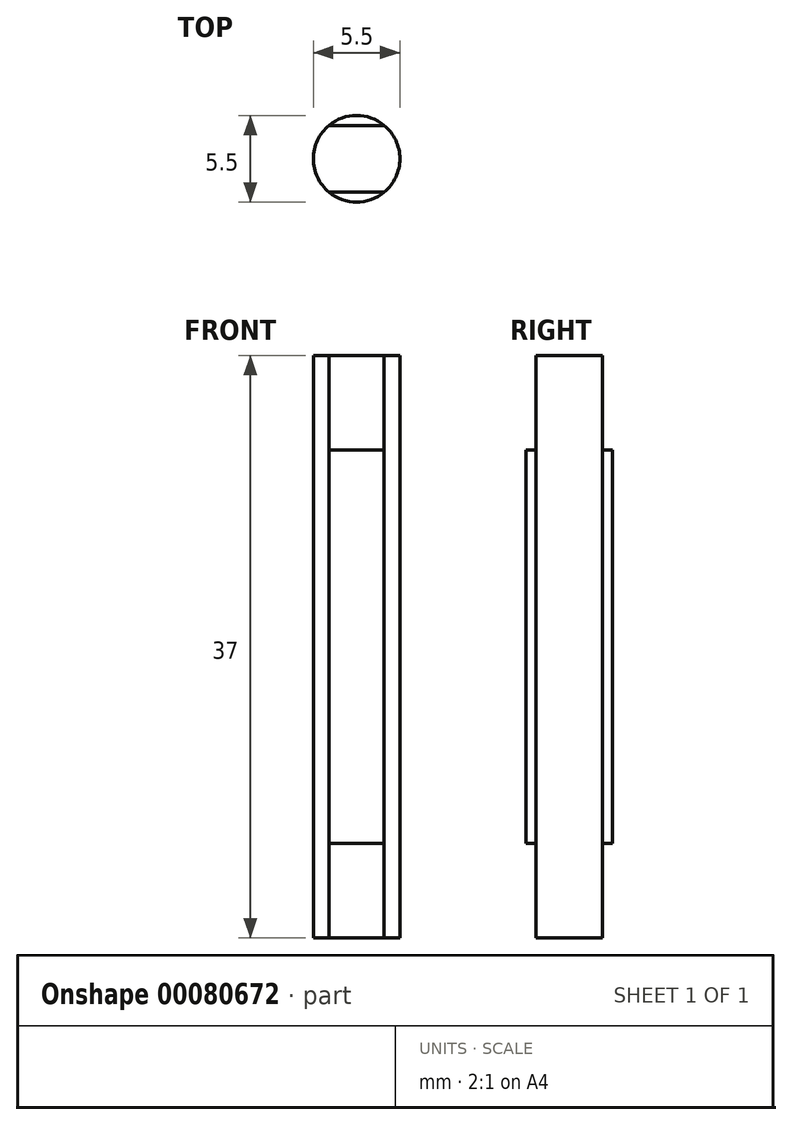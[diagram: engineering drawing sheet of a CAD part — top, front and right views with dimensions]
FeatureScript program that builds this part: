
annotation { "Feature Type Name" : "Feature", "Feature Type Description" : "" }
export const myFeature = defineFeature(function(context is Context, id is Id, definition is map)
    precondition{}
    {
        {
            var Q0;
            Q0=qCreatedBy(makeId("Top.planeOp"),FACE);
            var sketch = newSketch(context, id + "F0", { "sketchPlane" : qUnion([Q0])});
            skCircle(sketch, "E0", {"center": v(0, 0) * mm, "radius": 2.75 * mm});
            skLineSegment(sketch, "E1.bottom", {"start": v(1.75, -2.12) * mm, "end": v(-1.75, -2.12) * mm});
            skLineSegment(sketch, "E1.top", {"start": v(1.75, 2.12) * mm, "end": v(-1.75, 2.12) * mm});
            skLineSegment(sketch, "E1.left", {"start": v(1.75, -2.12) * mm, "end": v(1.75, 2.12) * mm});
            skLineSegment(sketch, "E1.right", {"start": v(-1.75, -2.12) * mm, "end": v(-1.75, 2.12) * mm});
            skSolve(sketch);
        }
        {
            var Q0;
            {var subQ0=sQuery(id+"F0.wireOp",EDGE,"E1.top");Q0=makeQuery(id+"F0.imprint","IMPRINT",FACE,{"disambiguationData":[TD([[makeQuery(id+"F0.imprint","IMPRINT",EDGE,{"derivedFrom":subQ0}),-1.0]])]});}
            var Q1;
            {var subQ0=sQuery(id+"F0.wireOp",EDGE,"E1.bottom");Q1=makeQuery(id+"F0.imprint","IMPRINT",FACE,{"disambiguationData":[TD([[makeQuery(id+"F0.imprint","IMPRINT",EDGE,{"derivedFrom":subQ0}),1.0]])]});}
            extrude(context, id + "F1", {"entities" : qUnion([Q0, Q1]), "depth" : 25 * mm, "symmetric" : true});
        }
        {
            var Q0;
            Q0=makeQuery(id+"F0.imprint","IMPRINT",FACE,{"disambiguationData":[TD([[makeQuery(id+"F0.imprint","IMPRINT",EDGE,{"derivedFrom":sQuery(id+"F0.wireOp",EDGE,"E1.bottom")}),-1.0]])]});
            var Q1;
            {var subQ0=sQuery(id+"F0.wireOp",EDGE,"E1.left");Q1=makeQuery(id+"F0.imprint","IMPRINT",FACE,{"disambiguationData":[TD([[makeQuery(id+"F0.imprint","IMPRINT",EDGE,{"derivedFrom":subQ0}),-1.0]])]});}
            var Q2;
            {var subQ0=sQuery(id+"F0.wireOp",EDGE,"E1.right");Q2=makeQuery(id+"F0.imprint","IMPRINT",FACE,{"disambiguationData":[TD([[makeQuery(id+"F0.imprint","IMPRINT",EDGE,{"derivedFrom":subQ0}),1.0]])]});}
            extrude(context, id + "F2", {"entities" : qUnion([Q0, Q1, Q2]), "depth" : 37 * mm, "symmetric" : true});
        }
    });
